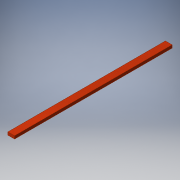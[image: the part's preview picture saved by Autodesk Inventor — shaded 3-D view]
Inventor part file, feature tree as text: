
AUTODESK INVENTOR PART (.ipt)
format: ipt  version: 2016 (Build 200138000, 138)  size: 92,160 bytes
history: native  units: in
note: dims shown in document units (in); Inventor stores cm internally (conversion verified against a paired STEP export)
features: extrude x1, sketch x1
ambient origin geometry x8: Origin, YZ Plane, XZ Plane, XY Plane, X Axis, Y Axis, Z Axis, Center Point
bodies: Solid1 (feature_tree)
feature tree (2):
  extrude  "Extrusion1"  Depth=82.25in
  sketch  "Sketch1"  dims[d0=1.5in d1=82.25in d2=3.5in d3=0.0in]
